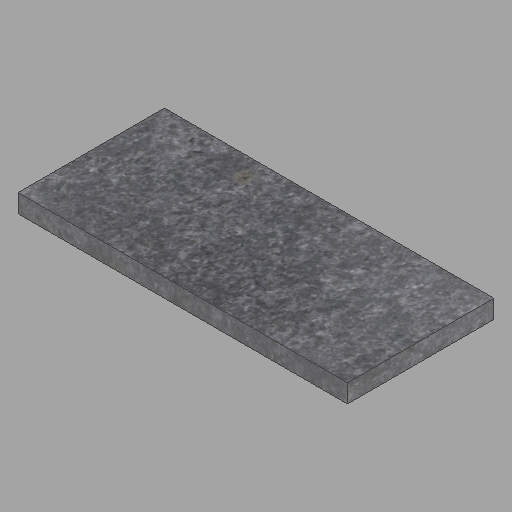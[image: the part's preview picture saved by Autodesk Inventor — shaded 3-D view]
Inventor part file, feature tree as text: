
AUTODESK INVENTOR PART (.ipt)
format: ipt  version: 2023 (Build 270158000, 158)  size: 226,304 bytes
history: native  units: in
note: dims shown in document units (in); Inventor stores cm internally (conversion verified against a paired STEP export)
features: other x1, extrude x1, sketch x1
ambient origin geometry x8: Origin, YZ Plane, XZ Plane, XY Plane, X Axis, Y Axis, Z Axis, Center Point
bodies: Solid1 (feature_tree)
feature tree (3):
  other  "2x16x36-28"
  extrude  "Extrusion1"  Depth=2.0in
  sketch  "Sketch1"  dims[d0=16.0in d1=2.0in d2=36.0in d3=0.0in]
